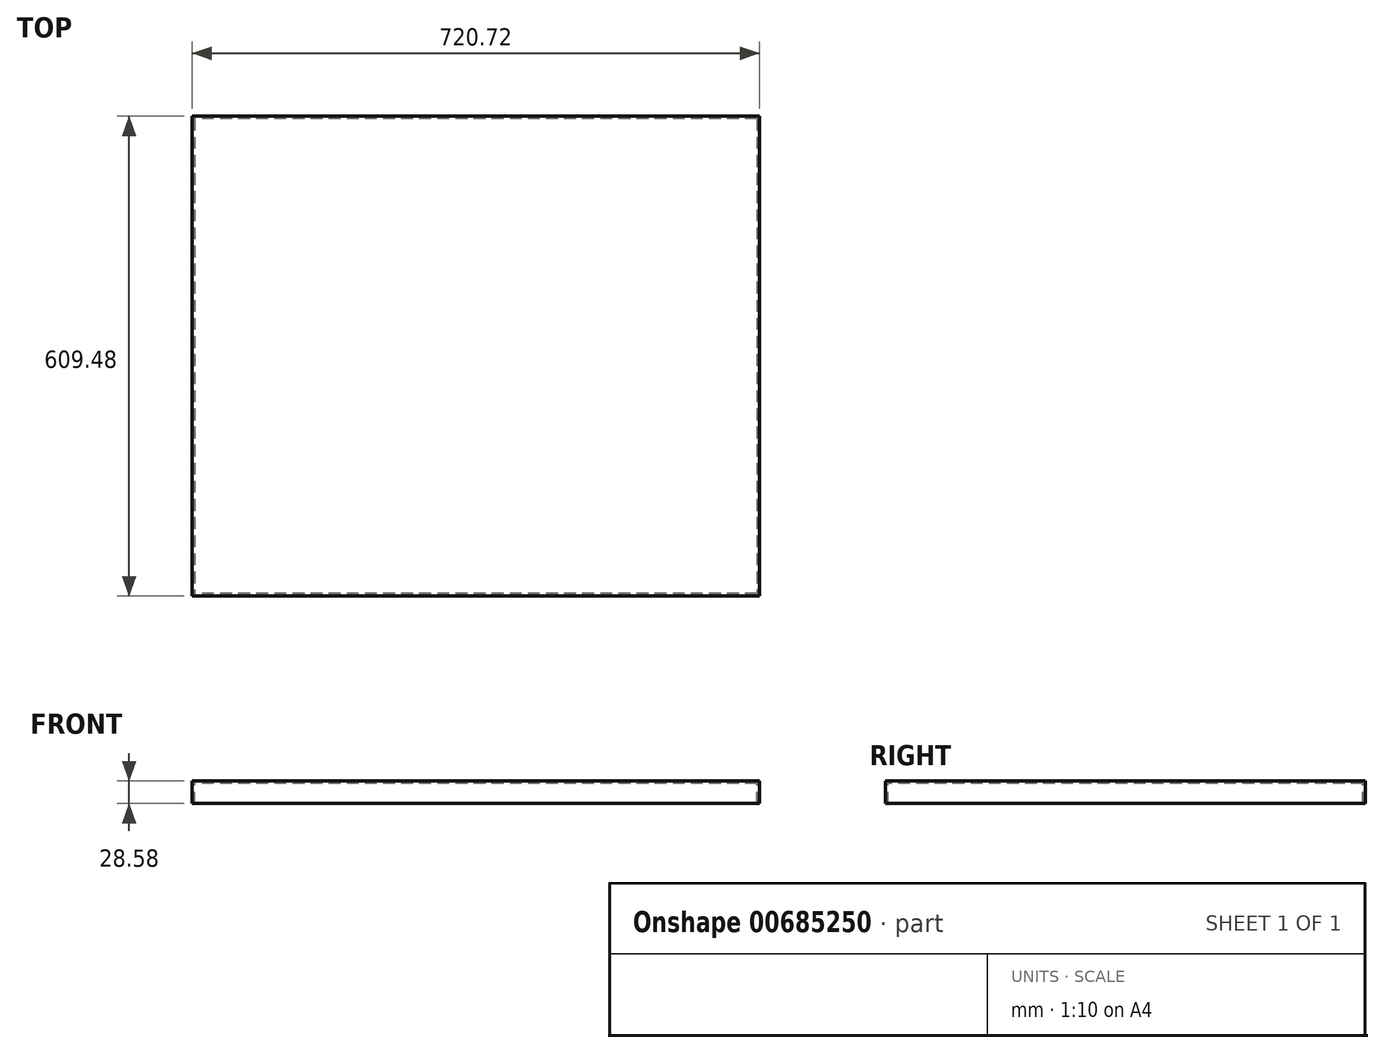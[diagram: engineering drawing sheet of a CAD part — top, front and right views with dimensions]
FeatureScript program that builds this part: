
annotation { "Feature Type Name" : "Feature", "Feature Type Description" : "" }
export const myFeature = defineFeature(function(context is Context, id is Id, definition is map)
    precondition{}
    {
        {
            var Q0;
            Q0=qCreatedBy(makeId("Top.planeOp"),FACE);
            var sketch = newSketch(context, id + "F0", { "sketchPlane" : qUnion([Q0])});
            skLineSegment(sketch, "E0.bottom", {"start": v(357.19, 301.56) * mm, "end": v(-357.19, 301.56) * mm});
            skLineSegment(sketch, "E0.top", {"start": v(357.19, -301.56) * mm, "end": v(-357.19, -301.56) * mm});
            skLineSegment(sketch, "E0.left", {"start": v(357.19, 301.56) * mm, "end": v(357.19, -301.56) * mm});
            skLineSegment(sketch, "E0.right", {"start": v(-357.19, 301.56) * mm, "end": v(-357.19, -301.56) * mm});
            skPoint(sketch, "E0.middle", {"position": v(0, 0) * mm});
            skSolve(sketch);
        }
        {
            var Q0;
            Q0 = qSketchRegion(id + "F0", true);
            extrude(context, id + "F1", {"entities" : qUnion([Q0]), "depth" : 3.17 * mm, "offsetDistance" : 25.4 * mm});
        }
        {
            var Q0;
            Q0=makeQuery(id+"F1.opExtrude","CAP_FACE",FACE,{"disambiguationData":[OSD([sQuery(id+"F0.wireOp",EDGE,"E0.bottom"),sQuery(id+"F0.wireOp",EDGE,"E0.top"),sQuery(id+"F0.wireOp",EDGE,"E0.left"),sQuery(id+"F0.wireOp",EDGE,"E0.right")])],"isStart":false});
            var sketch = newSketch(context, id + "F2", { "sketchPlane" : qUnion([Q0])});
            skLineSegment(sketch, "E1.top", {"start": v(-357.19, -301.56) * mm, "end": v(357.19, -301.56) * mm});
            skLineSegment(sketch, "E1.left", {"start": v(-357.19, 301.56) * mm, "end": v(-357.19, -301.56) * mm});
            skLineSegment(sketch, "E2.1", {"start": v(-360.36, 304.74) * mm, "end": v(-360.36, -304.74) * mm});
            skLineSegment(sketch, "E2.2", {"start": v(-360.36, -304.74) * mm, "end": v(360.36, -304.74) * mm});
            skLineSegment(sketch, "E2.3", {"start": v(360.36, 304.74) * mm, "end": v(360.36, -304.74) * mm});
            skLineSegment(sketch, "E3.bottom", {"start": v(-357.19, 301.56) * mm, "end": v(357.19, 301.56) * mm});
            skLineSegment(sketch, "E4", {"start": v(360.36, 304.74) * mm, "end": v(-360.36, 304.74) * mm});
            skLineSegment(sketch, "E5", {"start": v(357.19, 301.56) * mm, "end": v(357.19, -301.56) * mm});
            skSolve(sketch);
        }
        {
            var Q0;
            Q0 = qSketchRegion(id + "F2", true);
            extrude(context, id + "F3", {"entities" : qUnion([Q0]), "operationType" : NewBodyOperationType.ADD, "oppositeDirection" : true, "depth" : 28.57 * mm, "offsetDistance" : 25.4 * mm});
        }
    });
